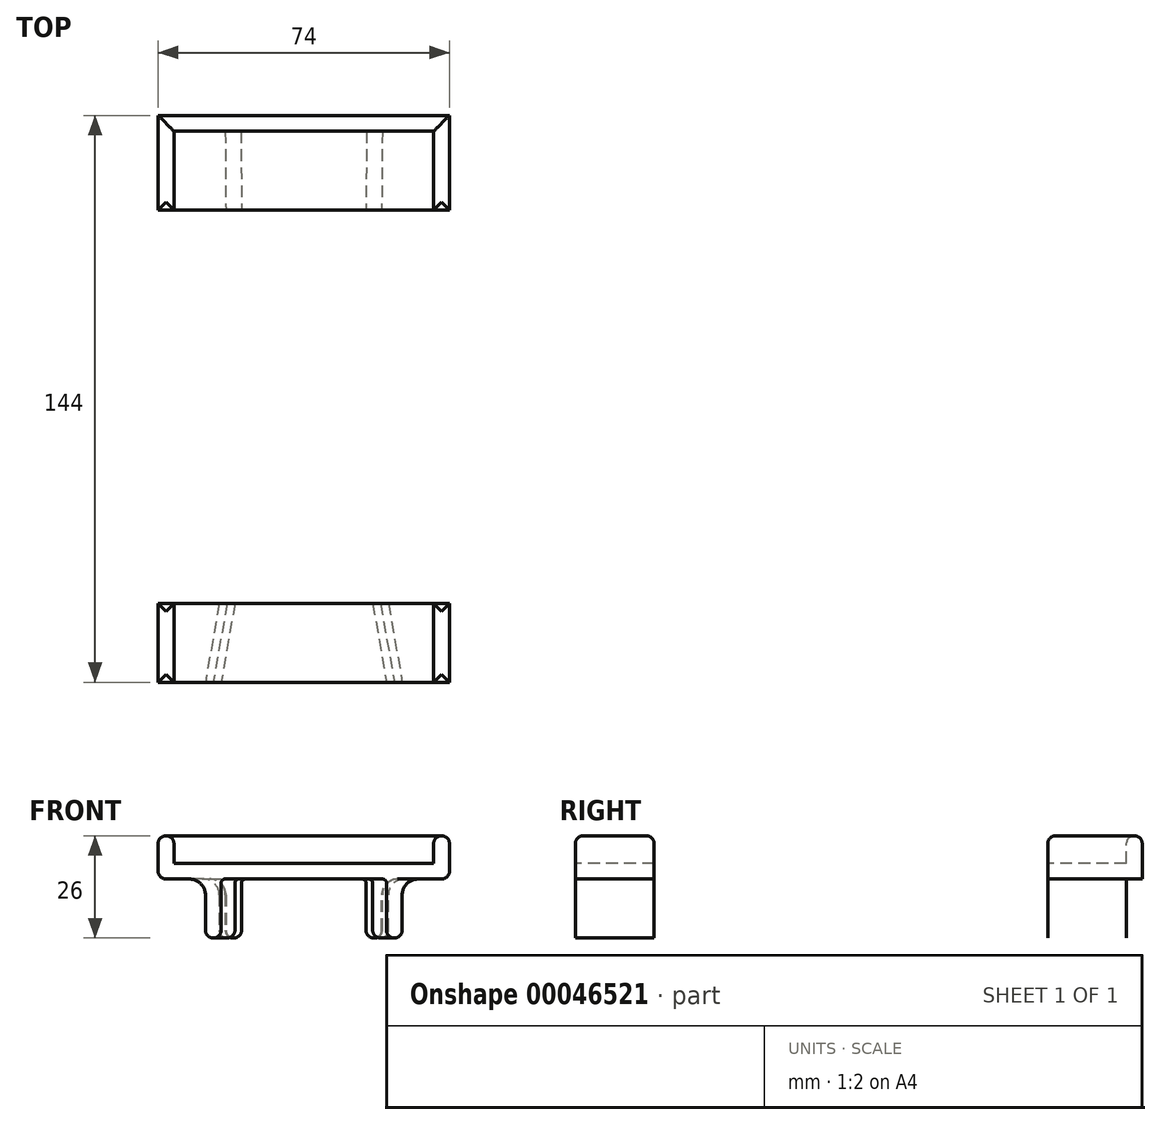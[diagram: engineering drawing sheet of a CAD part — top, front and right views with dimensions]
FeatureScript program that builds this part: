
annotation { "Feature Type Name" : "Feature", "Feature Type Description" : "" }
export const myFeature = defineFeature(function(context is Context, id is Id, definition is map)
    precondition{}
    {
        {
            var Q0;
            Q0=qCreatedBy(makeId("Front.planeOp"),FACE);
            var sketch = newSketch(context, id + "F0", { "sketchPlane" : qUnion([Q0])});
            skLineSegment(sketch, "E0", {"start": v(-37, 11) * mm, "end": v(-37, 0) * mm});
            skLineSegment(sketch, "E1", {"start": v(-37, 0) * mm, "end": v(-19.95, 0) * mm});
            skLineSegment(sketch, "E2", {"start": v(-19.95, 0) * mm, "end": v(-19.95, -15) * mm});
            skLineSegment(sketch, "E3", {"start": v(-19.95, -15) * mm, "end": v(-15.95, -15) * mm});
            skLineSegment(sketch, "E4", {"start": v(-15.95, -15) * mm, "end": v(-15.95, 0) * mm});
            skLineSegment(sketch, "E5", {"start": v(-15.95, 0) * mm, "end": v(15.95, 0) * mm});
            skLineSegment(sketch, "E6", {"start": v(15.95, 0) * mm, "end": v(15.95, -15) * mm});
            skLineSegment(sketch, "E7", {"start": v(15.95, -15) * mm, "end": v(19.95, -15) * mm});
            skLineSegment(sketch, "E8", {"start": v(19.95, -15) * mm, "end": v(19.95, 0) * mm});
            skLineSegment(sketch, "E9", {"start": v(19.95, 0) * mm, "end": v(37, 0) * mm});
            skLineSegment(sketch, "E10", {"start": v(37, 0) * mm, "end": v(37, 11) * mm});
            skLineSegment(sketch, "E11", {"start": v(37, 11) * mm, "end": v(33, 11) * mm});
            skLineSegment(sketch, "E12", {"start": v(33, 11) * mm, "end": v(33, 4) * mm});
            skLineSegment(sketch, "E13", {"start": v(33, 4) * mm, "end": v(-33, 4) * mm});
            skLineSegment(sketch, "E14", {"start": v(-33, 4) * mm, "end": v(-33, 11) * mm});
            skLineSegment(sketch, "E15", {"start": v(-33, 11) * mm, "end": v(-37, 11) * mm});
            skLineSegment(sketch, "E16", {"start": v(-19.95, 0) * mm, "end": v(-15.95, 0) * mm, "construction": true});
            skLineSegment(sketch, "E17", {"start": v(15.95, 0) * mm, "end": v(19.95, 0) * mm, "construction": true});
            skLineSegment(sketch, "E18", {"start": v(-33, 4) * mm, "end": v(-33, 0) * mm, "construction": true});
            skPoint(sketch, "E19", {"position": v(0, 4) * mm});
            skPoint(sketch, "E20", {"position": v(0, 0) * mm});
            skSolve(sketch);
        }
        {
            var Q0;
            Q0=qCreatedBy(makeId("Right.planeOp"),FACE);
            var sketch = newSketch(context, id + "F1", { "sketchPlane" : qUnion([Q0])});
            skPoint(sketch, "E21", {"position": v(0, 0) * mm});
            skLineSegment(sketch, "E22", {"start": v(-199.67, 0) * mm, "end": v(10.8, 0) * mm, "construction": true});
            skPoint(sketch, "E23", {"position": v(-20, 0) * mm});
            skPoint(sketch, "E24", {"position": v(-120, 0) * mm});
            skPoint(sketch, "E25", {"position": v(-140, 0) * mm});
            skSolve(sketch);
        }
        {
            var Q0;
            Q0=qCreatedBy(makeId("Front.planeOp"),FACE);
            var Q1;
            Q1=sQuery(id+"F1.wireOp",VERTEX,"E23");
            cPlane(context, id + "F2", {"entities" : qUnion([Q0, Q1]), "cplaneType" : CPlaneType.PLANE_POINT, "offset" : 150 * mm, "width" : 150 * mm, "height" : 150 * mm});
        }
        {
            var Q0;
            Q0=qCreatedBy(id+"F2.planeOp",FACE);
            var sketch = newSketch(context, id + "F3", { "sketchPlane" : qUnion([Q0])});
            skLineSegment(sketch, "E26", {"start": v(-37, 11) * mm, "end": v(-37, 0) * mm});
            skLineSegment(sketch, "E27", {"start": v(-37, 0) * mm, "end": v(-19.8, 0) * mm});
            skLineSegment(sketch, "E28", {"start": v(-19.8, 0) * mm, "end": v(-19.8, -15) * mm});
            skLineSegment(sketch, "E29", {"start": v(-19.8, -15) * mm, "end": v(-15.8, -15) * mm});
            skLineSegment(sketch, "E30", {"start": v(-15.8, -15) * mm, "end": v(-15.8, 0) * mm});
            skLineSegment(sketch, "E31", {"start": v(-15.8, 0) * mm, "end": v(15.8, 0) * mm});
            skLineSegment(sketch, "E32", {"start": v(15.8, 0) * mm, "end": v(15.8, -15) * mm});
            skLineSegment(sketch, "E33", {"start": v(15.8, -15) * mm, "end": v(19.8, -15) * mm});
            skLineSegment(sketch, "E34", {"start": v(19.8, -15) * mm, "end": v(19.8, 0) * mm});
            skLineSegment(sketch, "E35", {"start": v(19.8, 0) * mm, "end": v(37, 0) * mm});
            skLineSegment(sketch, "E36", {"start": v(37, 0) * mm, "end": v(37, 11) * mm});
            skLineSegment(sketch, "E37", {"start": v(37, 11) * mm, "end": v(33, 11) * mm});
            skLineSegment(sketch, "E38", {"start": v(33, 11) * mm, "end": v(33, 4) * mm});
            skLineSegment(sketch, "E39", {"start": v(33, 4) * mm, "end": v(-33, 4) * mm});
            skLineSegment(sketch, "E40", {"start": v(-33, 4) * mm, "end": v(-33, 11) * mm});
            skLineSegment(sketch, "E41", {"start": v(-33, 11) * mm, "end": v(-37, 11) * mm});
            skLineSegment(sketch, "E42", {"start": v(-19.8, 0) * mm, "end": v(-15.8, 0) * mm, "construction": true});
            skLineSegment(sketch, "E43", {"start": v(15.8, 0) * mm, "end": v(19.8, 0) * mm, "construction": true});
            skLineSegment(sketch, "E44", {"start": v(-33, 4) * mm, "end": v(-33, 0) * mm, "construction": true});
            skPoint(sketch, "E45", {"position": v(0, 4) * mm});
            skPoint(sketch, "E46", {"position": v(0, 0) * mm});
            skSolve(sketch);
        }
        {
            var Q0;
            Q0=qCreatedBy(makeId("Front.planeOp"),FACE);
            var Q1;
            Q1=sQuery(id+"F1.wireOp",VERTEX,"E24");
            cPlane(context, id + "F4", {"entities" : qUnion([Q0, Q1]), "cplaneType" : CPlaneType.PLANE_POINT, "offset" : 150 * mm, "width" : 150 * mm, "height" : 150 * mm});
        }
        {
            var Q0;
            Q0=qCreatedBy(makeId("Front.planeOp"),FACE);
            var Q1;
            Q1=sQuery(id+"F1.wireOp",VERTEX,"E25");
            cPlane(context, id + "F5", {"entities" : qUnion([Q0, Q1]), "cplaneType" : CPlaneType.PLANE_POINT, "offset" : 150 * mm, "width" : 150 * mm, "height" : 150 * mm});
        }
        {
            var Q0;
            Q0=qCreatedBy(id+"F4.planeOp",FACE);
            var sketch = newSketch(context, id + "F6", { "sketchPlane" : qUnion([Q0])});
            skLineSegment(sketch, "E47", {"start": v(-37, 11) * mm, "end": v(-37, 0) * mm});
            skLineSegment(sketch, "E48", {"start": v(-37, 0) * mm, "end": v(-21.5, 0) * mm});
            skLineSegment(sketch, "E49", {"start": v(-21.5, 0) * mm, "end": v(-21.5, -15) * mm});
            skLineSegment(sketch, "E50", {"start": v(-21.5, -15) * mm, "end": v(-17.5, -15) * mm});
            skLineSegment(sketch, "E51", {"start": v(-17.5, -15) * mm, "end": v(-17.5, 0) * mm});
            skLineSegment(sketch, "E52", {"start": v(-17.5, 0) * mm, "end": v(17.5, 0) * mm});
            skLineSegment(sketch, "E53", {"start": v(17.5, 0) * mm, "end": v(17.5, -15) * mm});
            skLineSegment(sketch, "E54", {"start": v(17.5, -15) * mm, "end": v(21.5, -15) * mm});
            skLineSegment(sketch, "E55", {"start": v(21.5, -15) * mm, "end": v(21.5, 0) * mm});
            skLineSegment(sketch, "E56", {"start": v(21.5, 0) * mm, "end": v(37, 0) * mm});
            skLineSegment(sketch, "E57", {"start": v(37, 0) * mm, "end": v(37, 11) * mm});
            skLineSegment(sketch, "E58", {"start": v(37, 11) * mm, "end": v(33, 11) * mm});
            skLineSegment(sketch, "E59", {"start": v(33, 11) * mm, "end": v(33, 4) * mm});
            skLineSegment(sketch, "E60", {"start": v(33, 4) * mm, "end": v(-33, 4) * mm});
            skLineSegment(sketch, "E61", {"start": v(-33, 4) * mm, "end": v(-33, 11) * mm});
            skLineSegment(sketch, "E62", {"start": v(-33, 11) * mm, "end": v(-37, 11) * mm});
            skLineSegment(sketch, "E63", {"start": v(-21.5, 0) * mm, "end": v(-17.5, 0) * mm, "construction": true});
            skLineSegment(sketch, "E64", {"start": v(17.5, 0) * mm, "end": v(21.5, 0) * mm, "construction": true});
            skLineSegment(sketch, "E65", {"start": v(-33, 4) * mm, "end": v(-33, 0) * mm, "construction": true});
            skPoint(sketch, "E66", {"position": v(0, 4) * mm});
            skPoint(sketch, "E67", {"position": v(0, 0) * mm});
            skSolve(sketch);
        }
        {
            var Q0;
            Q0=qCreatedBy(id+"F5.planeOp",FACE);
            var sketch = newSketch(context, id + "F7", { "sketchPlane" : qUnion([Q0])});
            skLineSegment(sketch, "E68", {"start": v(-37, 11) * mm, "end": v(-37, 0) * mm});
            skLineSegment(sketch, "E69", {"start": v(-37, 0) * mm, "end": v(-25, 0) * mm});
            skLineSegment(sketch, "E70", {"start": v(-25, 0) * mm, "end": v(-25, -15) * mm});
            skLineSegment(sketch, "E71", {"start": v(-25, -15) * mm, "end": v(-21, -15) * mm});
            skLineSegment(sketch, "E72", {"start": v(-21, -15) * mm, "end": v(-21, 0) * mm});
            skLineSegment(sketch, "E73", {"start": v(-21, 0) * mm, "end": v(21, 0) * mm});
            skLineSegment(sketch, "E74", {"start": v(21, 0) * mm, "end": v(21, -15) * mm});
            skLineSegment(sketch, "E75", {"start": v(21, -15) * mm, "end": v(25, -15) * mm});
            skLineSegment(sketch, "E76", {"start": v(25, -15) * mm, "end": v(25, 0) * mm});
            skLineSegment(sketch, "E77", {"start": v(25, 0) * mm, "end": v(37, 0) * mm});
            skLineSegment(sketch, "E78", {"start": v(37, 0) * mm, "end": v(37, 11) * mm});
            skLineSegment(sketch, "E79", {"start": v(37, 11) * mm, "end": v(33, 11) * mm});
            skLineSegment(sketch, "E80", {"start": v(33, 11) * mm, "end": v(33, 4) * mm});
            skLineSegment(sketch, "E81", {"start": v(33, 4) * mm, "end": v(-33, 4) * mm});
            skLineSegment(sketch, "E82", {"start": v(-33, 4) * mm, "end": v(-33, 11) * mm});
            skLineSegment(sketch, "E83", {"start": v(-33, 11) * mm, "end": v(-37, 11) * mm});
            skLineSegment(sketch, "E84", {"start": v(-25, 0) * mm, "end": v(-21, 0) * mm, "construction": true});
            skLineSegment(sketch, "E85", {"start": v(21, 0) * mm, "end": v(25, 0) * mm, "construction": true});
            skLineSegment(sketch, "E86", {"start": v(-33, 4) * mm, "end": v(-33, 0) * mm, "construction": true});
            skPoint(sketch, "E87", {"position": v(0, 4) * mm});
            skPoint(sketch, "E88", {"position": v(0, 0) * mm});
            skSolve(sketch);
        }
        {
            var Q0;
            Q0=makeQuery(id+"F0.imprint","IMPRINT",FACE,{"disambiguationData":[TD([[makeQuery(id+"F0.imprint","IMPRINT",EDGE,{"derivedFrom":sQuery(id+"F0.wireOp",EDGE,"E0")}),1.0]])]});
            var Q1;
            Q1=makeQuery(id+"F3.imprint","IMPRINT",FACE,{"disambiguationData":[TD([[makeQuery(id+"F3.imprint","IMPRINT",EDGE,{"derivedFrom":sQuery(id+"F3.wireOp",EDGE,"E26")}),1.0]])]});
            loft(context, id + "F8", {"sheetProfilesArray" : [{ "sheetProfileEntities" : qUnion([Q0]) }, { "sheetProfileEntities" : qUnion([Q1]) }]});
        }
        {
            var Q0;
            Q0=makeQuery(id+"F6.imprint","IMPRINT",FACE,{"disambiguationData":[TD([[makeQuery(id+"F6.imprint","IMPRINT",EDGE,{"derivedFrom":sQuery(id+"F6.wireOp",EDGE,"E47")}),1.0]])]});
            var Q1;
            Q1=makeQuery(id+"F7.imprint","IMPRINT",FACE,{"disambiguationData":[TD([[makeQuery(id+"F7.imprint","IMPRINT",EDGE,{"derivedFrom":sQuery(id+"F7.wireOp",EDGE,"E68")}),1.0]])]});
            loft(context, id + "F9", {"sheetProfilesArray" : [{ "sheetProfileEntities" : qUnion([Q0]) }, { "sheetProfileEntities" : qUnion([Q1]) }]});
        }
        {
            var Q0;
            Q0=makeQuery(id+"F8.opLoft","CAP_FACE",FACE,{"disambiguationData":[OSD([makeQuery(id+"F0.imprint","IMPRINT",FACE,{"disambiguationData":[TD([[makeQuery(id+"F0.imprint","IMPRINT",EDGE,{"derivedFrom":sQuery(id+"F0.wireOp",EDGE,"E0")}),1.0]])]})])],"isStart":true});
            var sketch = newSketch(context, id + "F10", { "sketchPlane" : qUnion([Q0])});
            skLineSegment(sketch, "E89.bottom", {"start": v(37, 11) * mm, "end": v(-37, 11) * mm});
            skLineSegment(sketch, "E89.top", {"start": v(37, 0) * mm, "end": v(-37, 0) * mm});
            skLineSegment(sketch, "E89.left", {"start": v(37, 11) * mm, "end": v(37, 0) * mm});
            skLineSegment(sketch, "E89.right", {"start": v(-37, 11) * mm, "end": v(-37, 0) * mm});
            skSolve(sketch);
        }
        {
            var Q0;
            Q0 = qSketchRegion(id + "F10", true);
            extrude(context, id + "F11", {"entities" : qUnion([Q0]), "operationType" : NewBodyOperationType.ADD, "depth" : 4 * mm});
        }
        {
            var Q0;
            Q0=makeQuery(id+"F11.boolean.opBoolean","MERGE",FACE,{"derivedFrom":[makeQuery(id+"F8.opLoft","SWEPT_FACE",FACE,{"disambiguationData":[OSD([sQuery(id+"F0.wireOp",EDGE,"E0"),sQuery(id+"F0.wireOp",EDGE,"E14"),sQuery(id+"F0.wireOp",EDGE,"E15"),sQuery(id+"F3.wireOp",EDGE,"E26"),sQuery(id+"F3.wireOp",EDGE,"E40"),sQuery(id+"F3.wireOp",EDGE,"E41")])]}),makeQuery(id+"F8.opLoft","SWEPT_FACE",FACE,{"disambiguationData":[OSD([sQuery(id+"F0.wireOp",EDGE,"E10"),sQuery(id+"F0.wireOp",EDGE,"E11"),sQuery(id+"F0.wireOp",EDGE,"E12"),sQuery(id+"F3.wireOp",EDGE,"E36"),sQuery(id+"F3.wireOp",EDGE,"E37"),sQuery(id+"F3.wireOp",EDGE,"E38")])]}),makeQuery(id+"F11.opExtrude","SWEPT_FACE",FACE,{"disambiguationData":[OSD([sQuery(id+"F10.wireOp",EDGE,"E89.bottom")])]})]});
            var Q1;
            Q1=makeQuery(id+"F9.opLoft","SWEPT_FACE",FACE,{"disambiguationData":[OSD([sQuery(id+"F6.wireOp",EDGE,"E47"),sQuery(id+"F6.wireOp",EDGE,"E61"),sQuery(id+"F6.wireOp",EDGE,"E62"),sQuery(id+"F7.wireOp",EDGE,"E68"),sQuery(id+"F7.wireOp",EDGE,"E82"),sQuery(id+"F7.wireOp",EDGE,"E83")])]});
            var Q2;
            Q2=makeQuery(id+"F9.opLoft","SWEPT_FACE",FACE,{"disambiguationData":[OSD([sQuery(id+"F6.wireOp",EDGE,"E57"),sQuery(id+"F6.wireOp",EDGE,"E58"),sQuery(id+"F6.wireOp",EDGE,"E59"),sQuery(id+"F7.wireOp",EDGE,"E78"),sQuery(id+"F7.wireOp",EDGE,"E79"),sQuery(id+"F7.wireOp",EDGE,"E80")])]});
            var Q3;
            Q3=makeQuery(id+"F11.boolean.opBoolean","MERGE",EDGE,{"derivedFrom":[makeQuery(id+"F8.opLoft","SWEPT_EDGE",EDGE,{"disambiguationData":[OSD([sQuery(id+"F0.wireOp",EDGE,"E0"),sQuery(id+"F0.wireOp",EDGE,"E1"),sQuery(id+"F3.wireOp",EDGE,"E26"),sQuery(id+"F3.wireOp",EDGE,"E27")])]}),makeQuery(id+"F11.opExtrude","SWEPT_EDGE",EDGE,{"disambiguationData":[OSD([sQuery(id+"F10.wireOp",EDGE,"E89.top"),sQuery(id+"F10.wireOp",EDGE,"E89.left")])]})]});
            var Q4;
            Q4=makeQuery(id+"F11.boolean.opBoolean","MERGE",EDGE,{"derivedFrom":[makeQuery(id+"F8.opLoft","SWEPT_EDGE",EDGE,{"disambiguationData":[OSD([sQuery(id+"F0.wireOp",EDGE,"E9"),sQuery(id+"F0.wireOp",EDGE,"E10"),sQuery(id+"F3.wireOp",EDGE,"E35"),sQuery(id+"F3.wireOp",EDGE,"E36")])]}),makeQuery(id+"F11.opExtrude","SWEPT_EDGE",EDGE,{"disambiguationData":[OSD([sQuery(id+"F10.wireOp",EDGE,"E89.top"),sQuery(id+"F10.wireOp",EDGE,"E89.right")])]})]});
            var Q5;
            Q5=makeQuery(id+"F9.opLoft","SWEPT_EDGE",EDGE,{"disambiguationData":[OSD([sQuery(id+"F6.wireOp",EDGE,"E47"),sQuery(id+"F6.wireOp",EDGE,"E48"),sQuery(id+"F7.wireOp",EDGE,"E68"),sQuery(id+"F7.wireOp",EDGE,"E69")])]});
            var Q6;
            Q6=makeQuery(id+"F9.opLoft","SWEPT_EDGE",EDGE,{"disambiguationData":[OSD([sQuery(id+"F6.wireOp",EDGE,"E56"),sQuery(id+"F6.wireOp",EDGE,"E57"),sQuery(id+"F7.wireOp",EDGE,"E77"),sQuery(id+"F7.wireOp",EDGE,"E78")])]});
            fillet(context, id + "F12", {"entities" : qUnion([Q0, Q1, Q2, Q3, Q4, Q5, Q6]), "radius" : 2 * mm, "allowEdgeOverflow" : false});
        }
        {
            var Q0;
            Q0=makeQuery(id+"F9.opLoft","SWEPT_EDGE",EDGE,{"disambiguationData":[OSD([sQuery(id+"F6.wireOp",EDGE,"E48"),sQuery(id+"F6.wireOp",EDGE,"E49"),sQuery(id+"F7.wireOp",EDGE,"E69"),sQuery(id+"F7.wireOp",EDGE,"E70")])]});
            var Q1;
            Q1=makeQuery(id+"F8.opLoft","SWEPT_EDGE",EDGE,{"disambiguationData":[OSD([sQuery(id+"F0.wireOp",EDGE,"E1"),sQuery(id+"F0.wireOp",EDGE,"E2"),sQuery(id+"F3.wireOp",EDGE,"E27"),sQuery(id+"F3.wireOp",EDGE,"E28")])]});
            var Q2;
            Q2=makeQuery(id+"F8.opLoft","SWEPT_EDGE",EDGE,{"disambiguationData":[OSD([sQuery(id+"F0.wireOp",EDGE,"E8"),sQuery(id+"F0.wireOp",EDGE,"E9"),sQuery(id+"F3.wireOp",EDGE,"E34"),sQuery(id+"F3.wireOp",EDGE,"E35")])]});
            var Q3;
            Q3=makeQuery(id+"F9.opLoft","SWEPT_EDGE",EDGE,{"disambiguationData":[OSD([sQuery(id+"F6.wireOp",EDGE,"E55"),sQuery(id+"F6.wireOp",EDGE,"E56"),sQuery(id+"F7.wireOp",EDGE,"E76"),sQuery(id+"F7.wireOp",EDGE,"E77")])]});
            fillet(context, id + "F13", {"entities" : qUnion([Q0, Q1, Q2, Q3]), "radius" : 4 * mm, "tangentPropagation" : true, "allowEdgeOverflow" : false});
        }
        {
            var Q0;
            Q0=makeQuery(id+"F9.opLoft","SWEPT_EDGE",EDGE,{"disambiguationData":[OSD([sQuery(id+"F6.wireOp",EDGE,"E51"),sQuery(id+"F6.wireOp",EDGE,"E52"),sQuery(id+"F7.wireOp",EDGE,"E72"),sQuery(id+"F7.wireOp",EDGE,"E73")])]});
            var Q1;
            Q1=makeQuery(id+"F9.opLoft","SWEPT_EDGE",EDGE,{"disambiguationData":[OSD([sQuery(id+"F6.wireOp",EDGE,"E52"),sQuery(id+"F6.wireOp",EDGE,"E53"),sQuery(id+"F7.wireOp",EDGE,"E73"),sQuery(id+"F7.wireOp",EDGE,"E74")])]});
            var Q2;
            Q2=makeQuery(id+"F8.opLoft","SWEPT_EDGE",EDGE,{"disambiguationData":[OSD([sQuery(id+"F0.wireOp",EDGE,"E5"),sQuery(id+"F0.wireOp",EDGE,"E6"),sQuery(id+"F3.wireOp",EDGE,"E31"),sQuery(id+"F3.wireOp",EDGE,"E32")])]});
            var Q3;
            Q3=makeQuery(id+"F8.opLoft","SWEPT_EDGE",EDGE,{"disambiguationData":[OSD([sQuery(id+"F0.wireOp",EDGE,"E4"),sQuery(id+"F0.wireOp",EDGE,"E5"),sQuery(id+"F3.wireOp",EDGE,"E30"),sQuery(id+"F3.wireOp",EDGE,"E31")])]});
            fillet(context, id + "F14", {"entities" : qUnion([Q0, Q1, Q2, Q3]), "radius" : 1 * mm, "tangentPropagation" : true, "allowEdgeOverflow" : false});
        }
        {
            var Q0;
            Q0=makeQuery(id+"F9.opLoft","SWEPT_EDGE",EDGE,{"disambiguationData":[OSD([sQuery(id+"F6.wireOp",EDGE,"E50"),sQuery(id+"F6.wireOp",EDGE,"E51"),sQuery(id+"F7.wireOp",EDGE,"E71"),sQuery(id+"F7.wireOp",EDGE,"E72")])]});
            var Q1;
            Q1=makeQuery(id+"F9.opLoft","SWEPT_EDGE",EDGE,{"disambiguationData":[OSD([sQuery(id+"F6.wireOp",EDGE,"E49"),sQuery(id+"F6.wireOp",EDGE,"E50"),sQuery(id+"F7.wireOp",EDGE,"E70"),sQuery(id+"F7.wireOp",EDGE,"E71")])]});
            var Q2;
            Q2=makeQuery(id+"F9.opLoft","SWEPT_EDGE",EDGE,{"disambiguationData":[OSD([sQuery(id+"F6.wireOp",EDGE,"E53"),sQuery(id+"F6.wireOp",EDGE,"E54"),sQuery(id+"F7.wireOp",EDGE,"E74"),sQuery(id+"F7.wireOp",EDGE,"E75")])]});
            var Q3;
            Q3=makeQuery(id+"F9.opLoft","SWEPT_EDGE",EDGE,{"disambiguationData":[OSD([sQuery(id+"F6.wireOp",EDGE,"E54"),sQuery(id+"F6.wireOp",EDGE,"E55"),sQuery(id+"F7.wireOp",EDGE,"E75"),sQuery(id+"F7.wireOp",EDGE,"E76")])]});
            var Q4;
            Q4=makeQuery(id+"F8.opLoft","SWEPT_EDGE",EDGE,{"disambiguationData":[OSD([sQuery(id+"F0.wireOp",EDGE,"E6"),sQuery(id+"F0.wireOp",EDGE,"E7"),sQuery(id+"F3.wireOp",EDGE,"E32"),sQuery(id+"F3.wireOp",EDGE,"E33")])]});
            var Q5;
            Q5=makeQuery(id+"F8.opLoft","SWEPT_EDGE",EDGE,{"disambiguationData":[OSD([sQuery(id+"F0.wireOp",EDGE,"E7"),sQuery(id+"F0.wireOp",EDGE,"E8"),sQuery(id+"F3.wireOp",EDGE,"E33"),sQuery(id+"F3.wireOp",EDGE,"E34")])]});
            var Q6;
            Q6=makeQuery(id+"F8.opLoft","SWEPT_EDGE",EDGE,{"disambiguationData":[OSD([sQuery(id+"F0.wireOp",EDGE,"E3"),sQuery(id+"F0.wireOp",EDGE,"E4"),sQuery(id+"F3.wireOp",EDGE,"E29"),sQuery(id+"F3.wireOp",EDGE,"E30")])]});
            var Q7;
            Q7=makeQuery(id+"F8.opLoft","SWEPT_EDGE",EDGE,{"disambiguationData":[OSD([sQuery(id+"F0.wireOp",EDGE,"E2"),sQuery(id+"F0.wireOp",EDGE,"E3"),sQuery(id+"F3.wireOp",EDGE,"E28"),sQuery(id+"F3.wireOp",EDGE,"E29")])]});
            fillet(context, id + "F15", {"entities" : qUnion([Q0, Q1, Q2, Q3, Q4, Q5, Q6, Q7]), "radius" : 2 * mm, "tangentPropagation" : true, "allowEdgeOverflow" : false});
        }
    });
